# Revit family: Seating-Casual-Naughtone-Viv_Lounge_Chair
name_source: partatom
category: Furniture
revit_build: Autodesk Revit Architecture 2014 (Build: 20140709_2115(x64)
units: mm (PartAtom-declared; Revit-internal decimal feet)

## types (2) — shared parameters
Additional Materials = Additional material and finish options available. Please contact Naughtone direct for further information.
Base Options = Chromed mild steel base as standard. White powder coated steel frame and other RAL colours available on request. Please contact Naughtone direct for further information.
COBie Description = Designed by Naughtone, The Viv chair's paired down shape is highlighted by its tight upholstery, cleverly held deeply in to the bucketed seat. Viv was motivated by quality and function and the range of chair, barstool and lounge chair are a welcome addition to any space, especially as their fully upholstered form can be easily altered with a change of fabrics.
Current Revision = 1
Depth = 650 mm  [stored 2.13255 ft]
Description = Viv Lounge Chair
Height = 650 mm  [stored 2.13255 ft]
Length = 595 mm  [stored 1.9521 ft]
Manufacturer = Naughtone
Model = Viv Lounge Chair
Name = Furniture-Seating-Casual-Naughtone-Viv
Product URL = http://www.naughtone.com
Type Comments = Stacking Chairs
TypeName = 595mmx650mmx650mm, Viv Lounge Chair
URL = http://www.naughtone.com
Uniclass = Pr_40_50_12_82
WarrantyDuration = 60
zero-valued in all types: Barcode, Cost, SerialNumber, TagNumber

## per-type parameters (varying)
| type | Base Option | Option | Sled Base | Swivel Base |
| VIV-LO-SL | Yes | Sled Base | Yes | No |
| VIV-LO-SW | No | Swivel Base | No | Yes |

note: column(s) folded — value = type name in every type: AssetIdentifier, Product Code

note: [stored X ft] marks values corroborated as IEEE doubles in the binary element streams (Revit-internal decimal feet)

## geometry (parser evidence)
native form markers: Sweep x5
no freeform markers — native parametric forms only
